# Revit family: Faucet-Wall_Mount-Lavatory-KOHLER-COMPOSED-K-73061T_1
name_source: partatom
category: Plumbing Fixtures
revit_build: Autodesk Revit 2017 (Build: 20160225_1515(x64)
units: mm (PartAtom-declared; Revit-internal decimal feet)

## family parameters
Cut with Voids When Loaded = No
Host = Face
OmniClass Number = 23.31.11.00
Part Type = Normal
Room Calculation Point = No
Round Connector Dimension = Use Diameter
Shared = No

## types (1)
- Not a Type-See Type Catalog
    ADA Compliant = No
    Assembly Code = D2010
    CW Connection = Yes
    Cold Water Inlet = Cold Water Inlet
    Date Modified = 09/22/2020
    Default Elevation = 36"
    Description = Bai Shi single-handle wall outlet basin faucet
    Drain Included = Yes
    Finish = Default
    Flow Rate = 0 GPM
    HW Connection = Yes
    Handle Clearance = 0"
    Height = 3 5/16"
    Hot Water Inlet = Hot Water Inlet
    Length = 6 5/8"
    Manufacturer = KOHLER Co.
    Master Format 2014 = 22 41 39
    Master Format 2014 Name = Residential Faucets, Supplies, and Trim
    Material = Premium Metal Construction
    Pressure = 0.00 psi
    Product Documentation Link = https://files.kohler.com.cn
    Product Name = COMPOSED
    Product Page URL = https://www.kohler.com.cn
    Spout Reach = 6 5/8"
    Type = 0
    URL = http://www.kohler.com.cn
    Vent Connection = No
    Waste Connection = No
    Waste Water Outlet = Waste Water Outlet
    WaterSense Certified = No
    Width = 9 1/16"

## geometry (parser evidence)
native form markers: Sweep x3
no freeform markers — native parametric forms only
